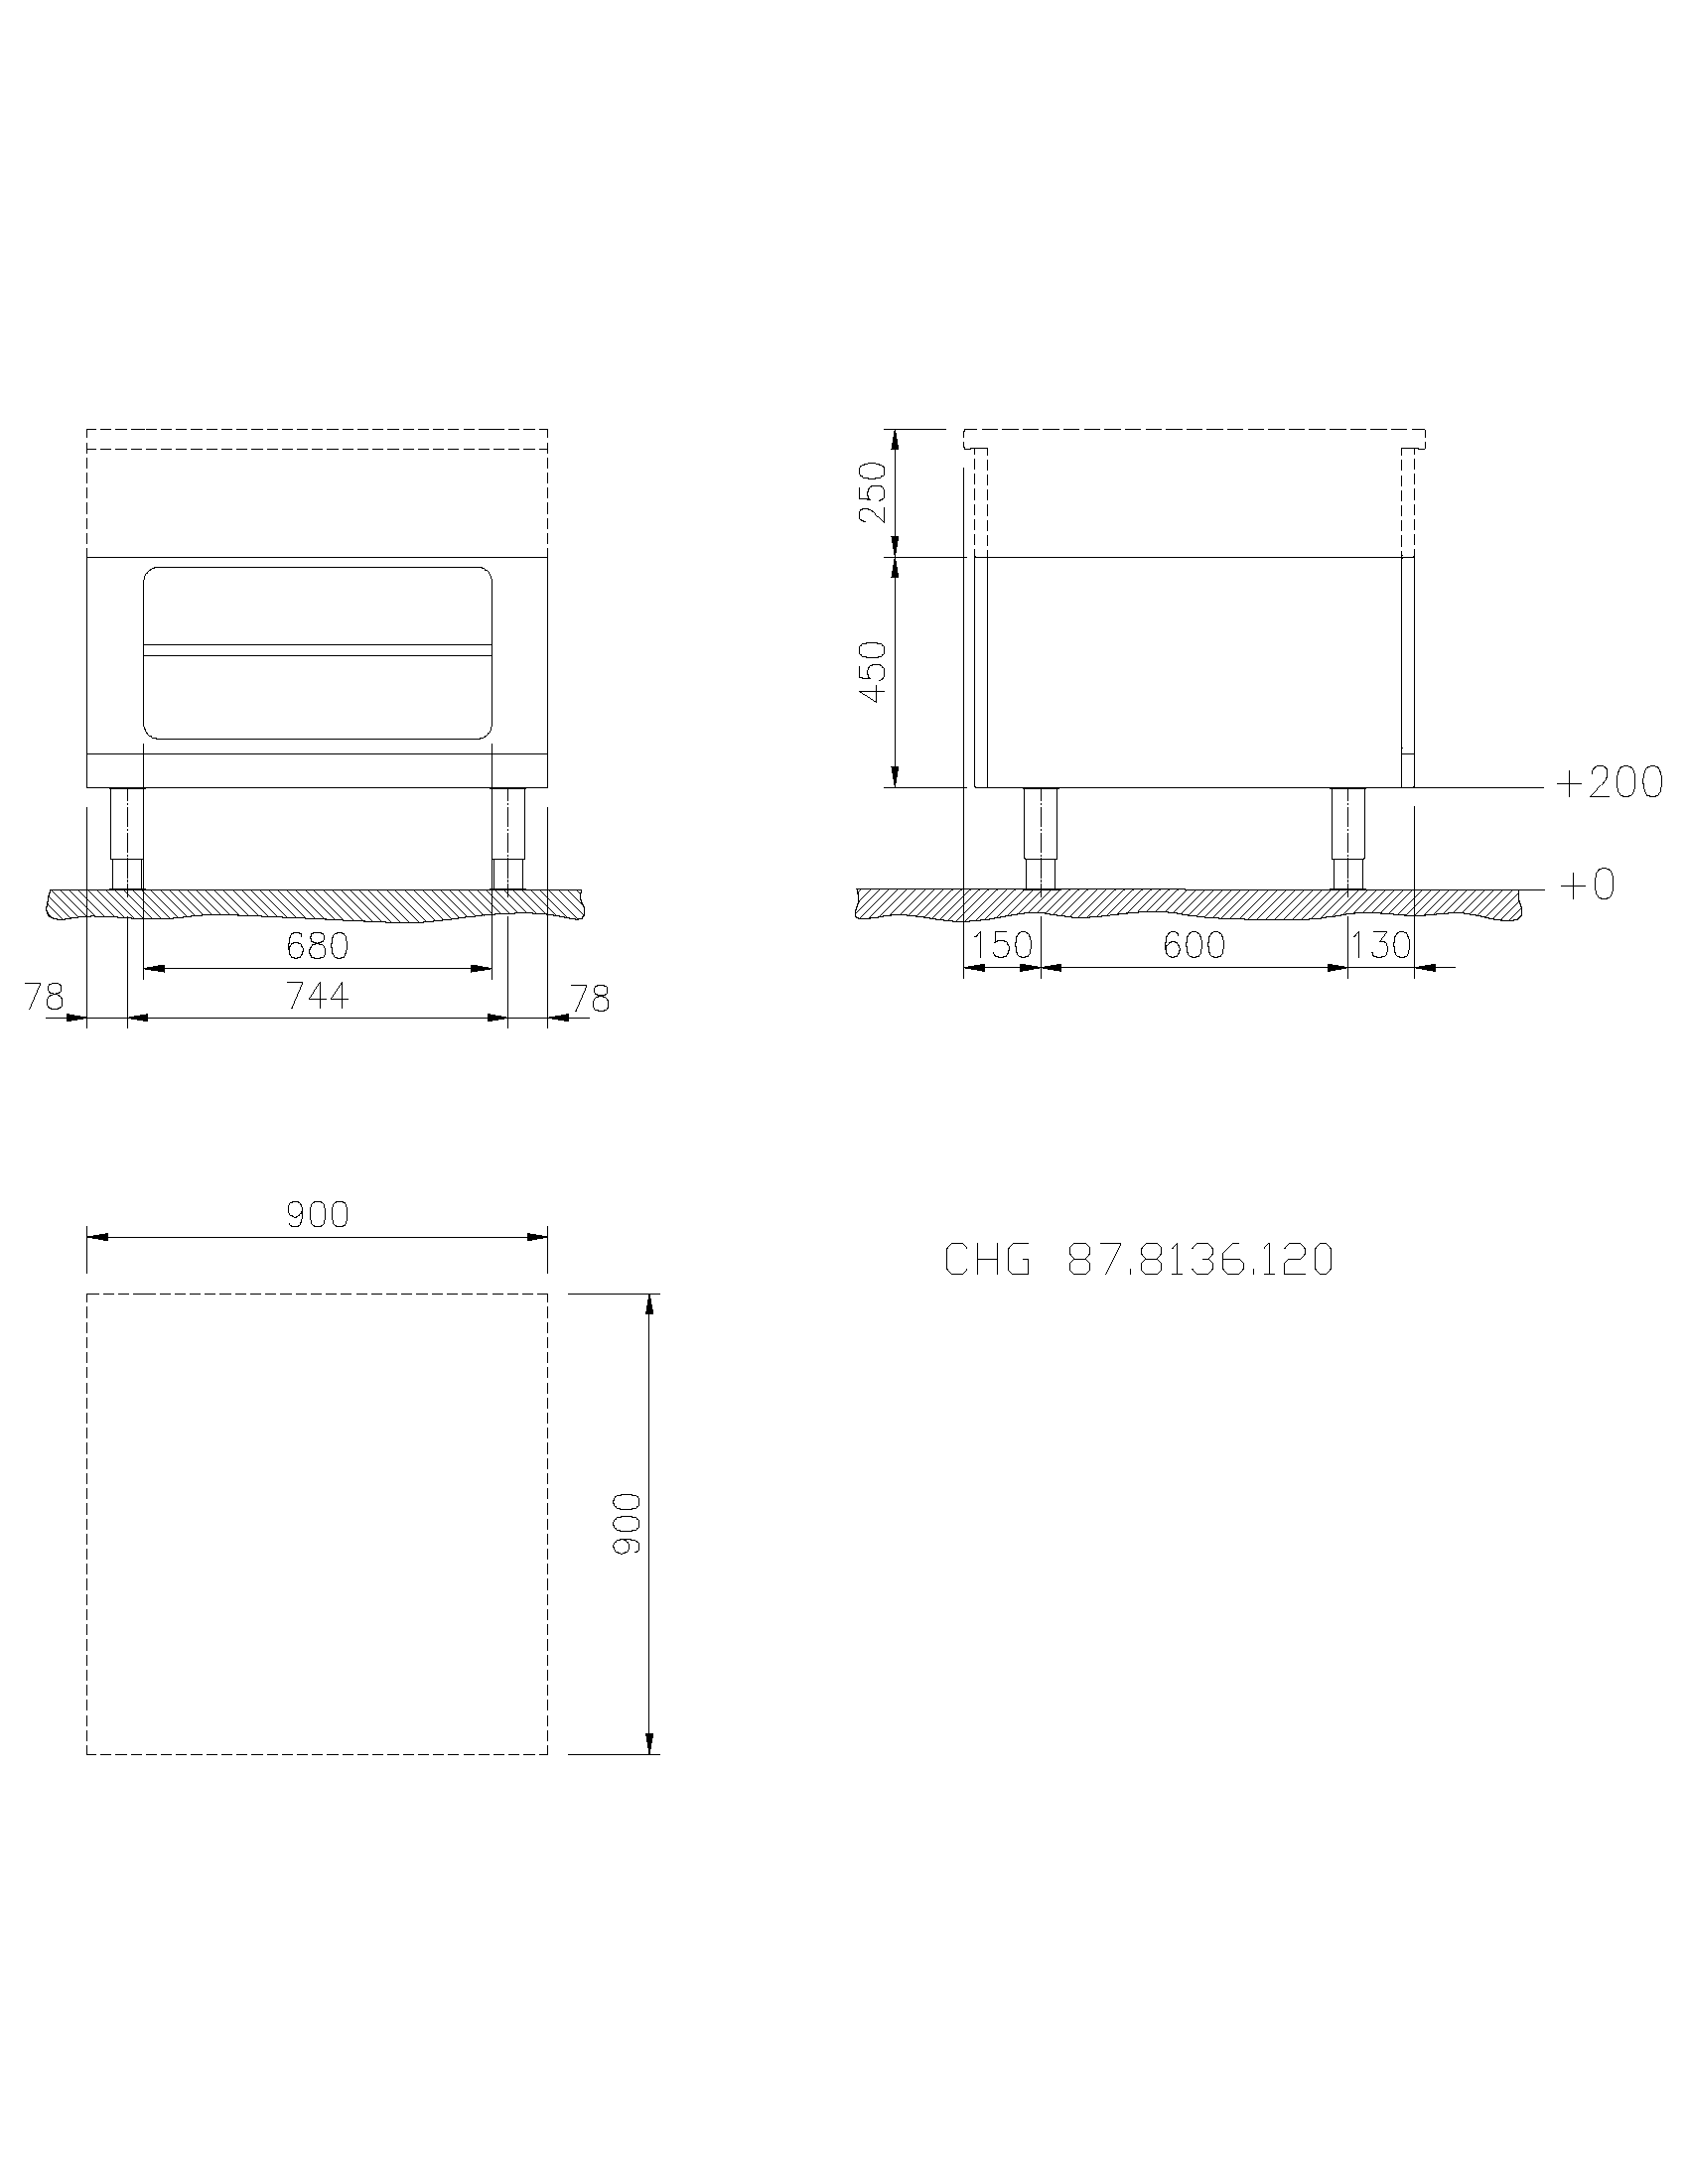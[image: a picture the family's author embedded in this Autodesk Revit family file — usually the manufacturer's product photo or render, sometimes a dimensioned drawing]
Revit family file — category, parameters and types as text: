
# Revit family: QF_ELECTROLUXPROFESSIONAL_589823_MCBGEAE1DM
name_source: partatom
category: Attrezzature speciali
units: mm (PartAtom-declared; Revit-internal decimal feet)

## family parameters
Basato su piano di lavoro = No
Condiviso = No
Punto di calcolo locali = No
Quota connettore circolare = Usa diametro
Sempre verticale = Sì
Taglio con vuoti quando caricato = No
Tipo di parte = Normale

## types (1)
- Standard
    Accessory = Sì
    Cold Water Size = 1"
    Compressed Air Pressure = 0.00 psi
    Compressed Air Size = 0"
    Compressed Air Volume = 0 GPM
    Condensate Return Size = 0"
    Cycle = 50 Hz
    Depth Actual = 900 mm  [stored 2.95276 ft]
    Descrizione = BAINM,1/1GN,TAP(R)1S,500X900X700 MARINE
    Direct Waste Size = 1"
    Gas Input Pressure = 0.0
    Gas KW = 0
    Gas Size = 0"
    HP = 2 HP
    Height Actual = 700 mm  [stored 2.29659 ft]
    Hot Water Size = 1"
    Item Number = 589823
    Length Actual = 500 mm  [stored 1.64042 ft]
    Modello = MCBGEAE1DM
    Phase = 3
    Produttore = Electrolux Professional
    Prospetto di default = 0 mm  [stored 0 ft]
    Refrigerant Compressor Remote = Sì
    Refrigeration Liquid Line Size = 0 mm  [stored 0 ft]
    Refrigeration Suction Line Size = 0 mm  [stored 0 ft]
    Steam Consumption per Hour = 0
    Steam Supply Maximum Pressure = 0.00 psi
    Steam Supply Minimum Pressure = 0.00 psi
    Steam Supply Size = 0"
    URL = https://www.electroluxprofessional.com
    URL Manufacturer = https://www.electroluxprofessional.com
    Volts = 440 V
    Watts = 1500 W
    Weight = 44.00 kg

note: source unit labels omitted for Gas Input Pressure — the stored unit's dimension contradicts the parameter name (converter mislabeling)

note: [stored X ft] marks values corroborated as IEEE doubles in the binary element streams (Revit-internal decimal feet)

## geometry (parser evidence)
native form markers: Blend x2, Sweep x9
no freeform markers — native parametric forms only
